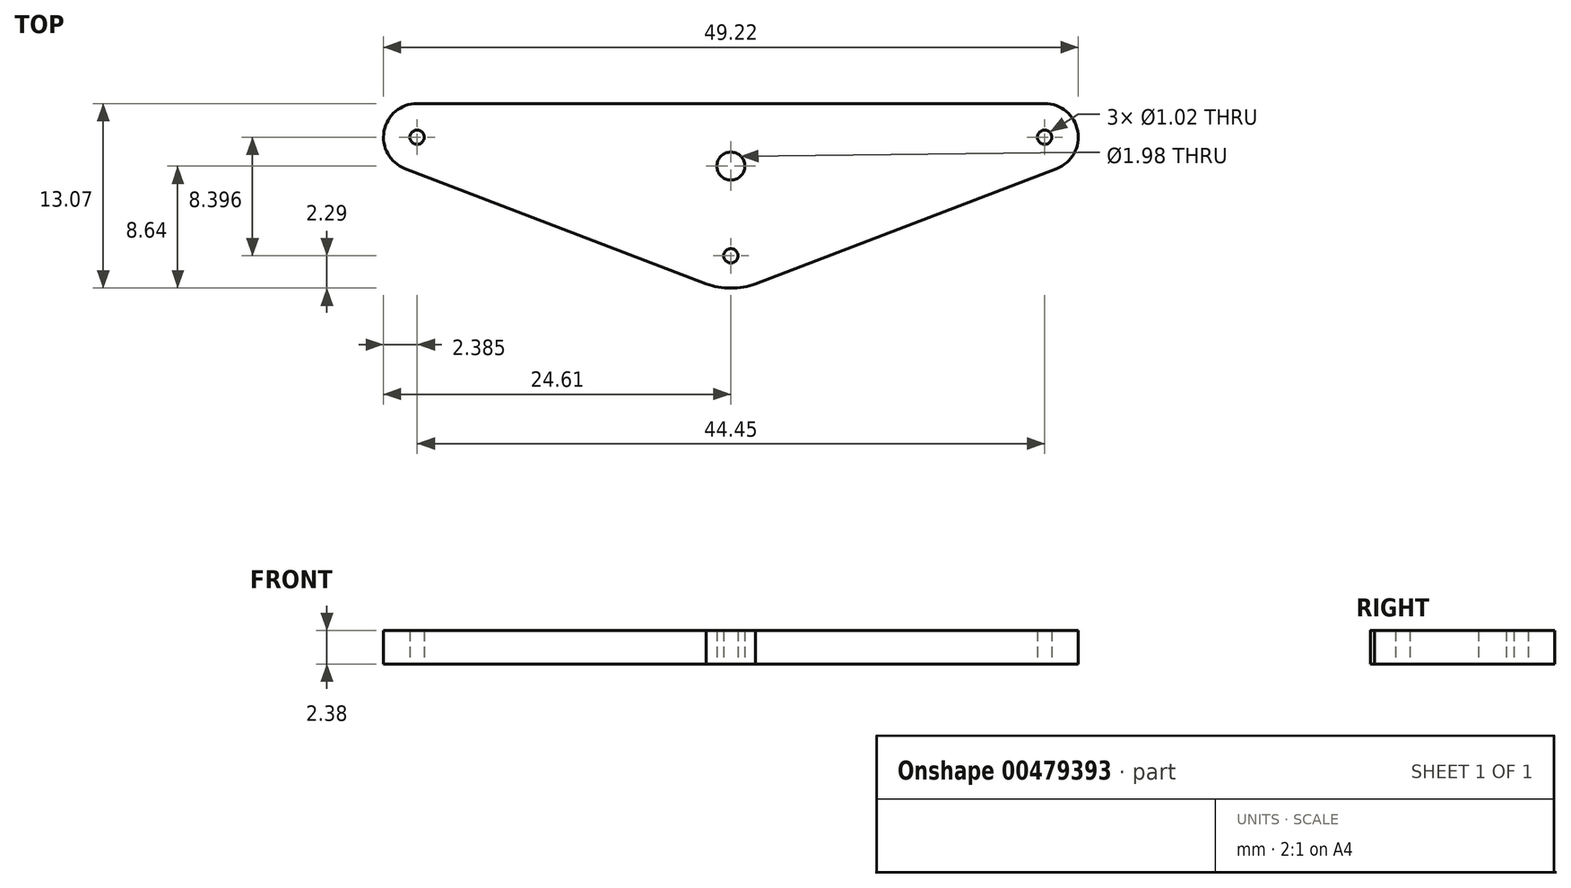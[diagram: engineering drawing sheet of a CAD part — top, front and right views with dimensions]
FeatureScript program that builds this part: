
annotation { "Feature Type Name" : "Feature", "Feature Type Description" : "" }
export const myFeature = defineFeature(function(context is Context, id is Id, definition is map)
    precondition{}
    {
        {
            var Q0;
            Q0=qCreatedBy(makeId("Top.planeOp"),FACE);
            var sketch = newSketch(context, id + "F0", { "sketchPlane" : qUnion([Q0])});
            skFitSpline(sketch, "E0.0", {"points": [v(26.79, 1.24) * mm, v(18.44, -1.95) * mm, v(10.1, -5.15) * mm, v(1.75, -8.35) * mm]});
            skArc(sketch, "E0.1", {"start": v(-1.75, -8.35) * mm, "mid": v(0, -8.64) * mm, "end": v(1.75, -8.35) * mm});
            skFitSpline(sketch, "E0.2", {"points": [v(-26.79, 1.24) * mm, v(-18.44, -1.95) * mm, v(-10.1, -5.15) * mm, v(-1.75, -8.35) * mm]});
            skArc(sketch, "E1", {"start": v(-22.22, 4.43) * mm, "mid": v(-24.57, 2.48) * mm, "end": v(-23.08, -0.18) * mm});
            skLineSegment(sketch, "E2", {"start": v(0, 0) * mm, "end": v(0, 4.43) * mm});
            skArc(sketch, "E3.MirrorC", {"start": v(22.22, 4.43) * mm, "mid": v(24.57, 2.48) * mm, "end": v(23.08, -0.18) * mm});
            skPoint(sketch, "E4.orphan", {"position": v(-28.84, 9.21) * mm});
            skPoint(sketch, "E5.orphan", {"position": v(25.77, 9.21) * mm});
            skCircle(sketch, "E6", {"center": v(0, -6.35) * mm, "radius": 0.5 * mm});
            skCircle(sketch, "E7", {"center": v(22.22, 2.05) * mm, "radius": 0.5 * mm});
            skCircle(sketch, "E8", {"center": v(-22.22, 2.05) * mm, "radius": 0.5 * mm});
            skLineSegment(sketch, "E9", {"start": v(22.23, 4.43) * mm, "end": v(-22.22, 4.43) * mm});
            skPoint(sketch, "E10.orphan", {"position": v(0, 8.23) * mm});
            skCircle(sketch, "E11", {"center": v(0, 0) * mm, "radius": 1 * mm});
            skSolve(sketch);
        }
        {
            var Q0;
            Q0 = qSketchRegion(id + "F0", true);
            extrude(context, id + "F1", {"entities" : qUnion([Q0]), "depth" : 2.38 * mm});
        }
    });
